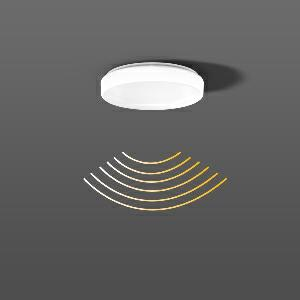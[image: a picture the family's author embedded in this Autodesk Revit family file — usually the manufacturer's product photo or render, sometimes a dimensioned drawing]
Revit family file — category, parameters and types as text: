
# Revit family: flat_polymero_kreis_slim_312084_002_4_19_b803
name_source: partatom
category: Lighting Fixtures
units: mm (PartAtom-declared; Revit-internal decimal feet)

## family parameters
Cut with Voids When Loaded = No
Host = Face
Light Source = No
Part Type = Normal
Room Calculation Point = No
Round Connector Dimension = Use Diameter
Shared = No

## types (1)
- FLAT POLYMERO KREIS SLIM (1 x LED Modul 840, 1300 lm, 4000)
    Apparent Load = 12 VA
    CIE Flux Codes = 43 73 92 88 100
    Color Rendering = 80
    Color Temperature = 4000
    Default Elevation = 1800 mm
    Description = Series: FLAT POLYMERO KREIS SLIM
Flat decorative round LED surface-mounted luminaire. Base: metal, powder-coated. Diffuser made of plastic (polycarbonate), opal, shockproof. Diffuser fastening: patented push system. Suitable for Ceiling mounting, Wall (surface). With integrated HF movement sensor. Functional parameters of a master luminaire (ceiling height of approx. 2.8 m): HF detector 24 GHz with integrated corridor function. Coverage: approx. 130° radial. Easy adjustment of functions via 3 associated push button switches. Sensitivity/Range: 0.5-5 m radial, adjustable from 10-100%. Time control 1 second to 15 minutes in 8 different levels. Daylight detection with 5 brightness levels and learning mode. Up to 9 slave luminaires can be operated with one master luminaire (max. up to 150 W / 230 W). Suitable for outdoor use to a limited extent only, as it is sensitive to all movements. 
Colour: white
Diameter: 300 mm
Height: 65 mm
Lamp: LED exchangeable
Socket: without socket
Colour temperature: 4000K
Colour rendering index (CRI): 83
System power: 12 W
Rated luminous flux: 1300 lm
Luminous efficiency: 108 lm/W
Control gear: Converter not necessary
Protection class: I
Type of protection: IP 40
    Height = 65 mm
    Lamp = 1 x LED Modul 840
    Lamp Light Flux = 1300 lm
    Lamp count = 1
    Length = 300 mm
    Lifetime = 50000 h
    Luminous efficacy = 108 lm/W
    Manufacturer = RZB
    ModVariant = No
    Model = 312084.002.4.19
    Mounting Place = Ceiling, Wall
    Mounting Type = Surface mounted
    Number of Poles = 1
    OnlyDefault = Yes
    Power Factor = 1
    Product Name = FLAT POLYMERO KREIS SLIM
    Product group = Surface mounted ceiling and wall luminaires
    ProductGroupID = 305
    Protection Class = Protection class I
    Protection Degree = IP 40
    RLX_Detail_Level = 1
    RLX_Emergency_Light_Flux = 0 lm
    RLX_Emergency_Type = 0
    RLX_Emergency_Type_DB = No
    RlxData = <blob elided: 71721 chars, md5=2aec7c93>
    Socket = socket
    Standby Power = 0 W
    System Light Flux = 1300 lm
    System Power = 12 W
    Type Comments = Product without accessories
    Type Image = 312084.002.1.19.jpg
    URL = http://relux.com
    VarID = ---
    Voltage = 230 V
    Voltage Range = 220-240 V
    Weight = 0.00 kg
    Width = 0 mm  [stored 0 ft]

note: [stored X ft] marks values corroborated as IEEE doubles in the binary element streams (Revit-internal decimal feet)

## geometry (parser evidence)
native form markers: Blend x4, Sweep x12
no freeform markers — native parametric forms only
